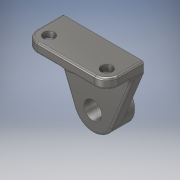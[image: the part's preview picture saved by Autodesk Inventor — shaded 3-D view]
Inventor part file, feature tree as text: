
AUTODESK INVENTOR PART (.ipt)
format: ipt  version: 2019 (Build 230136000, 136)  size: 335,360 bytes
history: native  units: mm
features: extrude x5, sketch x4, fillet x2, plane x1, rib x1
ambient origin geometry x8: Origin, YZ Plane, XZ Plane, XY Plane, X Axis, Y Axis, Z Axis, Center Point
bodies: Solid1 (feature_tree)
feature tree (13):
  extrude  "Extrusion1"  Depth=41.0mm
  sketch  "Sketch2"  dims[d2=18.0mm d3=22.0mm d4=0.0mm]
  extrude  "Extrusion2"  Depth=22.0mm TaperAngle=0.0deg
  extrude  "Extrusion3"  Depth=41.0mm
  plane  "Work Plane1"
  rib  "Rib1"
  sketch  "Sketch6"  dims[d7=10.0mm d8=10.0mm d9=0.0mm d10=27.0mm d11=0.0mm d12=-41.0mm d17=1.0mm d18=10.0mm d19=0.0mm d20=0.0mm d21=1.0mm d22=1.0mm d23=11.0mm d24=22.0mm d25=22.0mm d26=11.0mm d27=12.0mm d28=12.0mm d29=12.0mm d30=12.0mm d31=27.0mm d32=0.0mm d33=4.0mm d34=0.0mm d35=12.0mm d36=2.0mm]
  extrude  "Extrusion4"  Depth=10.0mm TaperAngle=0.0deg
  extrude  "Extrusion5"  Depth=2.0mm TaperAngle=0.0deg
  fillet  "Fillet1"  [1 undecoded]
  fillet  "Fillet2"  Radius=1.0mm
  sketch  "Sketch1"  dims[d0=40.0mm d1=41.0mm]
  sketch  "Sketch5"  dims[d5=82.0mm d6=41.0mm]
note: 1 required parameter value undecoded (feature->parameter linkage not recoverable at this tier; creation-order binding heuristic only, values carry confidence <= 0.55)
